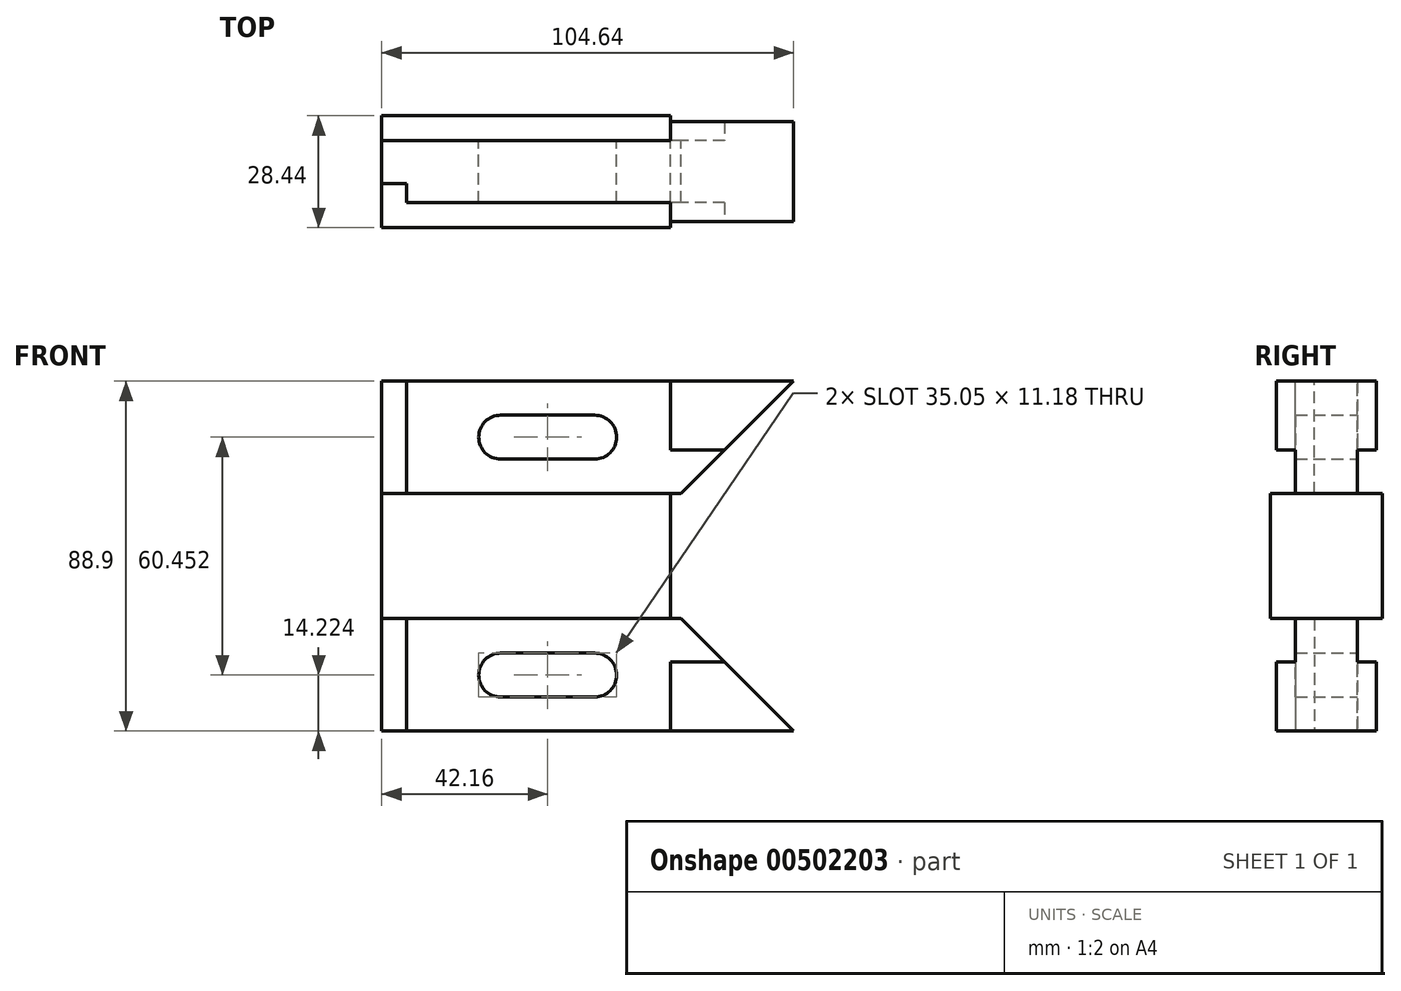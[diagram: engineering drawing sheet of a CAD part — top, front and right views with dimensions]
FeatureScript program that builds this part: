
annotation { "Feature Type Name" : "Feature", "Feature Type Description" : "" }
export const myFeature = defineFeature(function(context is Context, id is Id, definition is map)
    precondition{}
    {
        {
            var Q0;
            Q0=qCreatedBy(makeId("Front.planeOp"),FACE);
            var sketch = newSketch(context, id + "F0", { "sketchPlane" : qUnion([Q0])});
            skLineSegment(sketch, "E0.bottom", {"start": v(-52.32, 44.45) * mm, "end": v(52.32, 44.45) * mm});
            skLineSegment(sketch, "E0.top", {"start": v(-52.32, -44.45) * mm, "end": v(52.32, -44.45) * mm});
            skLineSegment(sketch, "E0.left", {"start": v(-52.32, 44.45) * mm, "end": v(-52.32, -44.45) * mm});
            skPoint(sketch, "E0.middle", {"position": v(0, 0) * mm});
            skLineSegment(sketch, "E1.0", {"start": v(-52.32, 15.88) * mm, "end": v(23.75, 15.88) * mm});
            skLineSegment(sketch, "E2.0", {"start": v(-52.32, -15.88) * mm, "end": v(23.75, -15.88) * mm});
            skLineSegment(sketch, "E3", {"start": v(-45.97, 44.45) * mm, "end": v(-45.97, 15.88) * mm});
            skLineSegment(sketch, "E4", {"start": v(-107.95, 0) * mm, "end": v(107.95, 0) * mm, "construction": true});
            skLineSegment(sketch, "E5", {"start": v(21.08, 15.88) * mm, "end": v(21.08, -15.88) * mm});
            skLineSegment(sketch, "E6", {"start": v(52.32, 44.45) * mm, "end": v(23.75, 15.88) * mm});
            skLineSegment(sketch, "E7", {"start": v(17.27, 44.45) * mm, "end": v(17.27, 26.92) * mm});
            skLineSegment(sketch, "E8", {"start": v(17.27, 26.92) * mm, "end": v(34.8, 26.92) * mm});
            skLineSegment(sketch, "E9.MirrorCS", {"start": v(52.32, -44.45) * mm, "end": v(23.75, -15.88) * mm});
            skLineSegment(sketch, "E10.MirrorCS", {"start": v(17.27, -26.92) * mm, "end": v(34.8, -26.92) * mm});
            skLineSegment(sketch, "E11.MirrorCS", {"start": v(17.27, -44.45) * mm, "end": v(17.27, -26.92) * mm});
            skLineSegment(sketch, "E12.MirrorCS", {"start": v(-45.97, -44.45) * mm, "end": v(-45.97, -15.88) * mm});
            skLineSegment(sketch, "E13", {"start": v(-22.1, -30.23) * mm, "end": v(1.78, -30.23) * mm, "construction": true});
            skArc(sketch, "E14.0.startCap", {"start": v(-22.1, -35.81) * mm, "mid": v(-27.69, -30.23) * mm, "end": v(-22.1, -24.64) * mm});
            skArc(sketch, "E14.0.endCap", {"start": v(1.78, -24.64) * mm, "mid": v(7.37, -30.23) * mm, "end": v(1.78, -35.81) * mm});
            skLineSegment(sketch, "E14.0.left", {"start": v(-22.1, -24.64) * mm, "end": v(1.78, -24.64) * mm});
            skLineSegment(sketch, "E14.0.right", {"start": v(-22.1, -35.81) * mm, "end": v(1.78, -35.81) * mm});
            skArc(sketch, "E15.MirrorCS", {"start": v(-22.1, 35.81) * mm, "mid": v(-27.69, 30.23) * mm, "end": v(-22.1, 24.64) * mm});
            skLineSegment(sketch, "E16.MirrorCS", {"start": v(-22.1, 24.64) * mm, "end": v(1.78, 24.64) * mm});
            skLineSegment(sketch, "E17.MirrorCS", {"start": v(-22.1, 30.23) * mm, "end": v(1.78, 30.23) * mm, "construction": true});
            skArc(sketch, "E18.MirrorCS", {"start": v(1.78, 24.64) * mm, "mid": v(7.37, 30.23) * mm, "end": v(1.78, 35.81) * mm});
            skLineSegment(sketch, "E19.MirrorCS", {"start": v(-22.1, 35.81) * mm, "end": v(1.78, 35.81) * mm});
            skSolve(sketch);
        }
        {
            var Q0;
            Q0 = qSketchRegion(id + "F0", true);
            extrude(context, id + "F1", {"entities" : qUnion([Q0]), "endBound" : BoundingType.SYMMETRIC, "depth" : 28.45 * mm});
        }
        {
            var Q0;
            Q0=makeQuery(id+"F1.opExtrude","SWEPT_FACE",FACE,{"disambiguationData":[OSD([sQuery(id+"F0.wireOp",EDGE,"E0.left")])]});
            cPlane(context, id + "F2", {"entities" : qUnion([Q0]), "cplaneType" : CPlaneType.OFFSET, "offset" : 25.4 * mm, "width" : 152.4 * mm, "height" : 152.4 * mm});
        }
        {
            var Q0;
            Q0=qCreatedBy(id+"F2.planeOp",FACE);
            var sketch = newSketch(context, id + "F3", { "sketchPlane" : qUnion([Q0])});
            skLineSegment(sketch, "E20.bottom", {"start": v(-14.22, 15.87) * mm, "end": v(14.22, 15.87) * mm});
            skLineSegment(sketch, "E20.top", {"start": v(-14.22, -15.87) * mm, "end": v(14.22, -15.87) * mm});
            skLineSegment(sketch, "E20.left", {"start": v(-14.22, 15.87) * mm, "end": v(-14.22, -15.87) * mm});
            skLineSegment(sketch, "E20.right", {"start": v(14.22, 15.87) * mm, "end": v(14.22, -15.87) * mm});
            skPoint(sketch, "E20.middle", {"position": v(0, 0) * mm});
            skLineSegment(sketch, "E21.0", {"start": v(14.22, 44.45) * mm, "end": v(-14.22, 44.45) * mm});
            skLineSegment(sketch, "E22.0", {"start": v(-14.22, 44.45) * mm, "end": v(-14.22, -44.45) * mm});
            skLineSegment(sketch, "E23.0", {"start": v(14.22, 44.45) * mm, "end": v(14.22, -44.45) * mm});
            skLineSegment(sketch, "E24.0", {"start": v(14.22, -44.45) * mm, "end": v(-14.22, -44.45) * mm});
            skLineSegment(sketch, "E25", {"start": v(-7.87, 15.87) * mm, "end": v(-7.87, 26.92) * mm});
            skLineSegment(sketch, "E26", {"start": v(-7.87, 26.92) * mm, "end": v(-12.7, 26.92) * mm});
            skLineSegment(sketch, "E27", {"start": v(-12.7, 26.92) * mm, "end": v(-12.7, 44.45) * mm});
            skLineSegment(sketch, "E28", {"start": v(-12.7, 44.45) * mm, "end": v(12.7, 44.45) * mm});
            skLineSegment(sketch, "E29", {"start": v(12.7, 44.45) * mm, "end": v(12.7, 26.92) * mm});
            skLineSegment(sketch, "E30", {"start": v(12.7, 26.92) * mm, "end": v(7.87, 26.92) * mm});
            skLineSegment(sketch, "E31", {"start": v(7.87, 26.92) * mm, "end": v(7.87, 15.87) * mm});
            skLineSegment(sketch, "E32", {"start": v(-31.93, 0) * mm, "end": v(31.93, 0) * mm, "construction": true});
            skPoint(sketch, "E32.endSnap0", {"position": v(-14.22, 0) * mm});
            skLineSegment(sketch, "E33.MirrorCS", {"start": v(7.87, -26.92) * mm, "end": v(7.87, -15.87) * mm});
            skLineSegment(sketch, "E34.MirrorCS", {"start": v(12.7, -26.92) * mm, "end": v(7.87, -26.92) * mm});
            skLineSegment(sketch, "E35.MirrorCS", {"start": v(-12.7, -26.92) * mm, "end": v(-12.7, -44.45) * mm});
            skLineSegment(sketch, "E36.MirrorCS", {"start": v(12.7, -44.45) * mm, "end": v(12.7, -26.92) * mm});
            skLineSegment(sketch, "E37.MirrorCS", {"start": v(-12.7, -44.45) * mm, "end": v(12.7, -44.45) * mm});
            skLineSegment(sketch, "E38.MirrorCS", {"start": v(-7.87, -15.87) * mm, "end": v(-7.87, -26.92) * mm});
            skLineSegment(sketch, "E39.MirrorCS", {"start": v(-7.87, -26.92) * mm, "end": v(-12.7, -26.92) * mm});
            skSolve(sketch);
        }
        {
            var Q0;
            {var subQ0=sQuery(id+"F3.wireOp",EDGE,"E25");Q0=makeQuery(id+"F3.imprint","IMPRINT",FACE,{"disambiguationData":[TD([[makeQuery(id+"F3.imprint","IMPRINT",EDGE,{"derivedFrom":subQ0}),1.0]])]});}
            var Q1;
            {var subQ0=sQuery(id+"F3.wireOp",EDGE,"E29");Q1=makeQuery(id+"F3.imprint","IMPRINT",FACE,{"disambiguationData":[TD([[makeQuery(id+"F3.imprint","IMPRINT",EDGE,{"derivedFrom":subQ0}),1.0]])]});}
            var Q2;
            {var subQ0=sQuery(id+"F3.wireOp",EDGE,"E35.MirrorCS");Q2=makeQuery(id+"F3.imprint","IMPRINT",FACE,{"disambiguationData":[TD([[makeQuery(id+"F3.imprint","IMPRINT",EDGE,{"derivedFrom":subQ0}),-1.0]])]});}
            var Q3;
            {var subQ3=sQuery(id+"F3.wireOp",EDGE,"E33.MirrorCS");Q3=makeQuery(id+"F3.imprint","IMPRINT",FACE,{"disambiguationData":[TD([[makeQuery(id+"F3.imprint","IMPRINT",EDGE,{"derivedFrom":subQ3}),-1.0]])]});}
            extrude(context, id + "F4", {"entities" : qUnion([Q0, Q1, Q2, Q3]), "operationType" : NewBodyOperationType.REMOVE, "endBound" : BoundingType.THROUGH_ALL, "oppositeDirection" : true, "depth" : 25.4 * mm});
        }
        {
            var Q0;
            Q0=makeQuery(id+"F1.opExtrude","SWEPT_FACE",FACE,{"disambiguationData":[OSD([sQuery(id+"F0.wireOp",EDGE,"E0.bottom")])]});
            cPlane(context, id + "F5", {"entities" : qUnion([Q0]), "cplaneType" : CPlaneType.OFFSET, "offset" : 19.8 * mm, "width" : 152.4 * mm, "height" : 152.4 * mm});
        }
        {
            var Q0;
            Q0=qCreatedBy(id+"F5.planeOp",FACE);
            var sketch = newSketch(context, id + "F6", { "sketchPlane" : qUnion([Q0])});
            skLineSegment(sketch, "E40.0", {"start": v(21.08, 14.22) * mm, "end": v(-52.32, 14.22) * mm});
            skLineSegment(sketch, "E41.0", {"start": v(21.08, -14.22) * mm, "end": v(-52.32, -14.22) * mm});
            skLineSegment(sketch, "E42", {"start": v(-52.32, 7.87) * mm, "end": v(21.08, 7.87) * mm});
            skLineSegment(sketch, "E43", {"start": v(-45.97, -7.87) * mm, "end": v(21.08, -7.87) * mm});
            skLineSegment(sketch, "E44", {"start": v(-52.32, -3.05) * mm, "end": v(-45.97, -3.05) * mm});
            skLineSegment(sketch, "E45", {"start": v(-45.97, -3.05) * mm, "end": v(-45.97, -7.87) * mm});
            skPoint(sketch, "E46.orphan", {"position": v(21.08, -7.87) * mm});
            skPoint(sketch, "E47.0.start.orphan", {"position": v(52.32, -12.7) * mm});
            skPoint(sketch, "E48.orphan", {"position": v(21.08, 7.87) * mm});
            skPoint(sketch, "E49.0.start.orphan", {"position": v(52.32, 12.7) * mm});
            skLineSegment(sketch, "E50", {"start": v(21.08, 14.22) * mm, "end": v(21.08, 7.87) * mm});
            skLineSegment(sketch, "E51", {"start": v(21.08, -7.87) * mm, "end": v(21.08, -14.22) * mm});
            skPoint(sketch, "E52.0.start.orphan", {"position": v(-52.32, -12.7) * mm});
            skLineSegment(sketch, "E53", {"start": v(-52.32, -3.05) * mm, "end": v(-52.32, -14.22) * mm});
            skPoint(sketch, "E54.trimOffspring.end.orphan", {"position": v(-52.32, 12.7) * mm});
            skLineSegment(sketch, "E55", {"start": v(-52.32, 14.22) * mm, "end": v(-52.32, 7.87) * mm});
            skSolve(sketch);
        }
        {
            var Q0;
            Q0=makeQuery(id+"F6.imprint","IMPRINT",FACE,{"disambiguationData":[TD([[makeQuery(id+"F6.imprint","IMPRINT",EDGE,{"derivedFrom":sQuery(id+"F6.wireOp",EDGE,"E41.0")}),-1.0]])]});
            var Q1;
            Q1=makeQuery(id+"F6.imprint","IMPRINT",FACE,{"disambiguationData":[TD([[makeQuery(id+"F6.imprint","IMPRINT",EDGE,{"derivedFrom":sQuery(id+"F6.wireOp",EDGE,"E40.0")}),1.0]])]});
            var Q2;
            {var subQ0=sQuery(id+"F3.wireOp",EDGE,"E20.bottom");Q2=makeQuery(id+"F4.boolean.opBoolean","COPY",FACE,{"derivedFrom":makeQuery(id+"F4.opExtrude","SWEPT_FACE",FACE,{"disambiguationData":[OSD([subQ0]),TDD([makeQuery(id+"F3.imprint","IMPRINT",EDGE,{"disambiguationData":[TD([[makeQuery(id+"F3.imprint","INTERSECT",VERTEX,{"derivedFrom":[subQ0,sQuery(id+"F3.wireOp",EDGE,"E23.0")]}),1.0]])],"derivedFrom":subQ0})])]})});}
            extrude(context, id + "F7", {"entities" : qUnion([Q0, Q1]), "operationType" : NewBodyOperationType.REMOVE, "endBound" : BoundingType.UP_TO_SURFACE, "oppositeDirection" : true, "endBoundEntityFace" : qUnion([Q2]), "depth" : 41.15 * mm});
        }
        {
            var Q0;
            Q0=makeQuery(id+"F1.opExtrude","SWEPT_FACE",FACE,{"disambiguationData":[OSD([sQuery(id+"F0.wireOp",EDGE,"E0.top")])]});
            cPlane(context, id + "F8", {"entities" : qUnion([Q0]), "cplaneType" : CPlaneType.OFFSET, "offset" : 25.4 * mm, "width" : 152.4 * mm, "height" : 152.4 * mm});
        }
        {
            var Q0;
            Q0=qCreatedBy(id+"F8.planeOp",FACE);
            var sketch = newSketch(context, id + "F9", { "sketchPlane" : qUnion([Q0])});
            skLineSegment(sketch, "E56.0", {"start": v(-52.32, -14.22) * mm, "end": v(-52.32, -7.87) * mm});
            skLineSegment(sketch, "E56.1", {"start": v(-52.32, 3.05) * mm, "end": v(-52.32, 14.22) * mm});
            skLineSegment(sketch, "E56.2", {"start": v(21.08, -14.22) * mm, "end": v(21.08, -7.87) * mm});
            skLineSegment(sketch, "E56.3", {"start": v(21.08, 7.87) * mm, "end": v(21.08, 14.22) * mm});
            skLineSegment(sketch, "E56.4", {"start": v(-52.32, 3.05) * mm, "end": v(-45.97, 3.05) * mm});
            skLineSegment(sketch, "E56.5", {"start": v(-45.97, 7.87) * mm, "end": v(21.08, 7.87) * mm});
            skLineSegment(sketch, "E56.6", {"start": v(21.08, -14.22) * mm, "end": v(-52.32, -14.22) * mm});
            skLineSegment(sketch, "E56.7", {"start": v(-45.97, 3.05) * mm, "end": v(-45.97, 7.87) * mm});
            skLineSegment(sketch, "E56.8", {"start": v(-52.32, -7.87) * mm, "end": v(21.08, -7.87) * mm});
            skLineSegment(sketch, "E56.9", {"start": v(21.08, 14.22) * mm, "end": v(-52.32, 14.22) * mm});
            skSolve(sketch);
        }
        {
            var Q0;
            Q0=makeQuery(id+"F9.imprint","IMPRINT",FACE,{"disambiguationData":[TD([[makeQuery(id+"F9.imprint","IMPRINT",EDGE,{"derivedFrom":sQuery(id+"F9.wireOp",EDGE,"E56.1")}),-1.0]])]});
            var Q1;
            Q1=makeQuery(id+"F9.imprint","IMPRINT",FACE,{"disambiguationData":[TD([[makeQuery(id+"F9.imprint","IMPRINT",EDGE,{"derivedFrom":sQuery(id+"F9.wireOp",EDGE,"E56.0")}),-1.0]])]});
            var Q2;
            {var subQ0=sQuery(id+"F3.wireOp",EDGE,"E20.top");Q2=makeQuery(id+"F4.boolean.opBoolean","COPY",FACE,{"derivedFrom":makeQuery(id+"F4.opExtrude","SWEPT_FACE",FACE,{"disambiguationData":[OSD([subQ0]),TDD([makeQuery(id+"F3.imprint","IMPRINT",EDGE,{"disambiguationData":[TD([[makeQuery(id+"F3.imprint","INTERSECT",VERTEX,{"derivedFrom":[sQuery(id+"F3.wireOp",EDGE,"E23.0"),subQ0]}),1.0]])],"derivedFrom":subQ0})])]})});}
            extrude(context, id + "F10", {"entities" : qUnion([Q0, Q1]), "operationType" : NewBodyOperationType.REMOVE, "endBound" : BoundingType.UP_TO_SURFACE, "oppositeDirection" : true, "endBoundEntityFace" : qUnion([Q2]), "depth" : 25.4 * mm});
        }
    });
